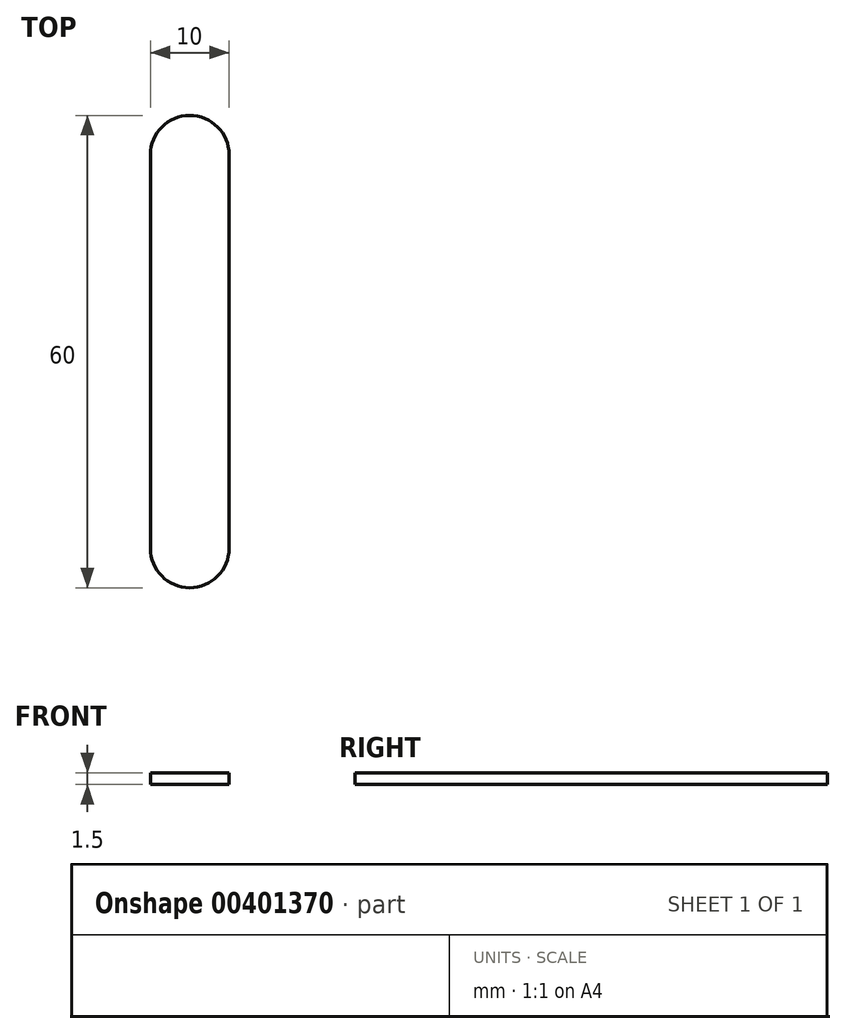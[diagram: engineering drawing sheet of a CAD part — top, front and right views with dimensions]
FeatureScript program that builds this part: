
annotation { "Feature Type Name" : "Feature", "Feature Type Description" : "" }
export const myFeature = defineFeature(function(context is Context, id is Id, definition is map)
    precondition{}
    {
        {
            var Q0;
            Q0=qCreatedBy(makeId("Top.planeOp"),FACE);
            var sketch = newSketch(context, id + "F0", { "sketchPlane" : qUnion([Q0])});
            skLineSegment(sketch, "E0", {"start": v(0, 25) * mm, "end": v(0, -25) * mm, "construction": true});
            skArc(sketch, "E1", {"start": v(5, 25) * mm, "mid": v(0, 30) * mm, "end": v(-5, 25) * mm});
            skLineSegment(sketch, "E2", {"start": v(2.5, 0) * mm, "end": v(-2.5, 0) * mm, "construction": true});
            skArc(sketch, "E3.MirrorC", {"start": v(5, -25) * mm, "mid": v(0, -30) * mm, "end": v(-5, -25) * mm});
            skLineSegment(sketch, "E4", {"start": v(-5, 25) * mm, "end": v(-5, -25) * mm});
            skLineSegment(sketch, "E5", {"start": v(5, 25) * mm, "end": v(5, -25) * mm});
            skSolve(sketch);
        }
        {
            var Q0;
            Q0 = qSketchRegion(id + "F0", true);
            extrude(context, id + "F1", {"entities" : qUnion([Q0]), "depth" : 1.5 * mm});
        }
    });
